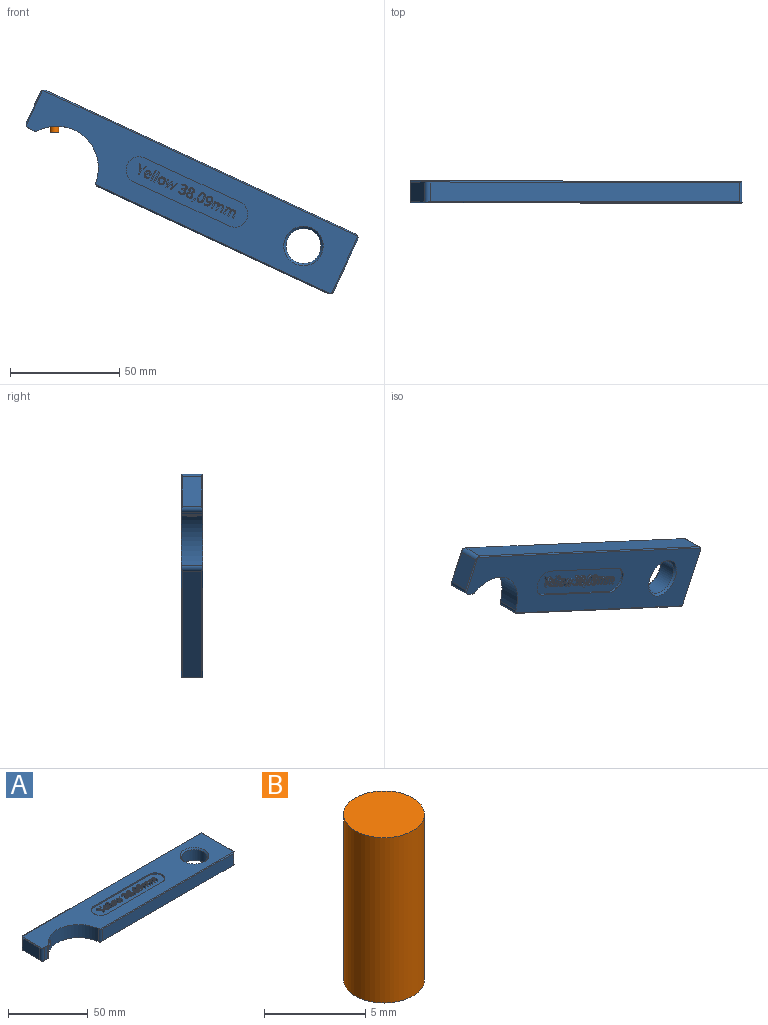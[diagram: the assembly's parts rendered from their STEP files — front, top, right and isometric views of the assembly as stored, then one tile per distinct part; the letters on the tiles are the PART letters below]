
ASSEMBLY  parts=2 mates=1
PART A: 291 faces, bbox 160x30x10 mm
  f0: cylinder r=19.04mm len=33.93mm, axis (0,0,-1), area 440.7mm2, adj f6,f7,f20,f25,f289
  f1: plane 60.11x12mm, normal (0,0,1), area 605.7mm2, adj f26,f27,f28,f29,f30,f31,f32,f33
  f2: plane 115.74x9mm, normal (0,-1,0), area 1041.6mm2, adj f10,f14,f20,f21
  f3: plane 26x9mm, normal (1,0,0), area 234mm2, adj f11,f15,f21,f22
  f4: plane 156x9mm, normal (0,1,0), area 1404mm2, adj f12,f16,f22,f23
  f5: plane 15x9mm, normal (-1,0,0), area 135mm2, adj f13,f17,f23,f24
  f6: plane 159x29mm, normal (0,0,1), area 3083.9mm2, adj f0,f8,f14,f15,f16,f17,f19,f20
  f7: plane 159x29mm, normal (0,0,-1), area 3774.3mm2, adj f0,f8,f10,f11,f12,f13,f18,f20
  f8: plane 10x2.76mm, normal (0,-1,0), area 27.6mm2, adj f6,f7,f24,f25
  f9: cylinder r=8mm len=16mm, axis (0,0,-1), area 402.1mm2, adj f18,f19
  f10: plane 118.38x0.5mm, normal (0,-0.71,-0.71), area 83.1mm2, adj f2,f7,f20,f21
  f11: plane 28.65x0.5mm, normal (0.71,0,-0.71), area 19.7mm2, adj f3,f7,f21,f22
  f12: plane 158.65x0.5mm, normal (0,0.71,-0.71), area 111.6mm2, adj f4,f7,f22,f23
  f13: plane 17.65x0.5mm, normal (-0.71,0,-0.71), area 11.9mm2, adj f5,f7,f23,f24
  f14: plane 118.38x0.5mm, normal (0,-0.71,0.71), area 83.1mm2, adj f2,f6,f20,f21
  f15: plane 28.65x0.5mm, normal (0.71,0,0.71), area 19.7mm2, adj f3,f6,f21,f22
  f16: plane 158.65x0.5mm, normal (0,0.71,0.71), area 111.6mm2, adj f4,f6,f22,f23
  f17: plane 17.65x0.5mm, normal (-0.71,0,0.71), area 11.9mm2, adj f5,f6,f23,f24
  f18: cone r=9mm half-angle=45deg, axis (0,0,-1), area 75.5mm2, adj f7,f9
  f19: cone r=8mm half-angle=45deg, axis (0,0,1), area 75.5mm2, adj f6,f9
  f20: cylinder r=2mm len=10mm, axis (0,0,-1), area 28.6mm2, adj f0,f2,f6,f7,f10,f14
  f21: cylinder r=2mm len=10mm, axis (0,0,1), area 29.5mm2, adj f2,f3,f6,f7,f10,f11,f14,f15
  f22: cylinder r=2mm len=10mm, axis (0,0,-1), area 29.5mm2, adj f3,f4,f6,f7,f11,f12,f15,f16
  f23: cylinder r=2mm len=10mm, axis (0,0,1), area 29.5mm2, adj f4,f5,f6,f7,f12,f13,f16,f17
  f24: cylinder r=2mm len=10mm, axis (0,0,1), area 30.5mm2, adj f5,f6,f7,f8,f13,f17
  f25: cylinder r=2mm len=10mm, axis (0,0,-1), area 18.1mm2, adj f0,f6,f7,f8
  f26: plane 48.11x1mm, normal (0,-1,0), area 48.1mm2, adj f1,f6,f27,f29
  f27: cylinder r=6mm len=12mm, axis (0,0,1), area 18.8mm2, adj f1,f6,f26,f28
  f28: plane 48.11x1mm, normal (0,1,0), area 48.1mm2, adj f1,f6,f27,f29
  f29: cylinder r=6mm len=12mm, axis (0,0,1), area 18.8mm2, adj f1,f6,f26,f28
  f30: plane 2.34x1.24mm, normal (-0.88,0.47,0), area 2.6mm2, adj f1,f31,f38,f39
  f31: plane 2.34x1.24mm, normal (0.88,0.47,0), area 2.6mm2, adj f1,f30,f32,f39
  f32: plane 1x0.59mm, normal (0,1,0), area 0.6mm2, adj f1,f31,f33,f39
  f33: plane 2.88x1.56mm, normal (-0.88,-0.47,0), area 3.3mm2, adj f1,f32,f34,f39
  f34: plane 1.79x1mm, normal (-1,0,0), area 1.8mm2, adj f1,f33,f35,f39
  f35: plane 1x0.55mm, normal (0,-1,0), area 0.5mm2, adj f1,f34,f36,f39
  f36: plane 1.81x1mm, normal (1,0,0), area 1.8mm2, adj f1,f35,f37,f39
  f37: plane 2.86x1.56mm, normal (0.88,-0.48,0), area 3.3mm2, adj f1,f36,f38,f39
  f38: plane 1x0.59mm, normal (0,1,0), area 0.6mm2, adj f1,f30,f37,f39
  f39: plane 4.67x3.66mm, normal (0,0,1), area 4.1mm2, adj f30,f31,f32,f33,f34,f35,f36,f37
  f40: extruded ~1x0.67mm, area 0.7mm2, adj f41,f58,f59,f60
  f41: extruded ~1x0.64mm, area 0.7mm2, adj f40,f42,f59,f60
  f42: extruded ~1x0.77mm, area 0.8mm2, adj f41,f43,f59,f60
  f43: plane 1.83x1mm, normal (0,1,0), area 1.8mm2, adj f42,f58,f59,f60
  f44: extruded ~1.22x1mm, area 1.4mm2, adj f1,f45,f57,f59
  f45: extruded ~1x0.61mm, area 0.6mm2, adj f1,f44,f46,f59
  f46: extruded ~1x0.53mm, area 0.6mm2, adj f1,f45,f47,f59
  f47: plane 1x0.47mm, normal (1,0,0), area 0.5mm2, adj f1,f46,f48,f59
  f48: extruded ~1.12x1mm, area 1.1mm2, adj f1,f47,f49,f59
  f49: extruded ~1x0.83mm, area 0.9mm2, adj f1,f48,f50,f59
  f50: extruded ~1x0.94mm, area 1mm2, adj f1,f49,f51,f59
  f51: plane 2.41x1mm, normal (0,-1,0), area 2.4mm2, adj f1,f50,f52,f59
  f52: plane 1x0.34mm, normal (1,0,0), area 0.3mm2, adj f1,f51,f53,f59
  f53: extruded ~1.14x1mm, area 1.2mm2, adj f1,f52,f54,f59
  f54: extruded ~1.04x1mm, area 1.2mm2, adj f1,f53,f55,f59
  f55: extruded ~1.12x1mm, area 1.3mm2, adj f1,f54,f56,f59
  f56: extruded ~1.35x1mm, area 1.4mm2, adj f1,f55,f57,f59
  f57: extruded ~1.31x1mm, area 1.4mm2, adj f1,f44,f56,f59
  f58: extruded ~1x0.76mm, area 0.8mm2, adj f40,f43,f59,f60
  f59: plane 3.63x2.96mm, normal (0,0,1), area 4.9mm2, adj f40,f41,f42,f43,f44,f45,f46,f47
  f60: plane 1.83x1.03mm, normal (0,0,1), area 1.5mm2, adj f40,f41,f42,f43,f58
  f61: plane 1x0.53mm, normal (0,-1,0), area 0.5mm2, adj f1,f62,f64,f65
  f62: plane 4.97x1mm, normal (1,0,0), area 5mm2, adj f1,f61,f63,f65
  f63: plane 1x0.53mm, normal (0,1,0), area 0.5mm2, adj f1,f62,f64,f65
  f64: plane 4.97x1mm, normal (-1,0,0), area 5mm2, adj f1,f61,f63,f65
  f65: plane 4.97x0.53mm, normal (0,0,1), area 2.6mm2, adj f61,f62,f63,f64
  f66: plane 1x0.53mm, normal (0,-1,0), area 0.5mm2, adj f1,f67,f69,f70
  f67: plane 4.97x1mm, normal (1,0,0), area 5mm2, adj f1,f66,f68,f70
  f68: plane 1x0.53mm, normal (0,1,0), area 0.5mm2, adj f1,f67,f69,f70
  f69: plane 4.97x1mm, normal (-1,0,0), area 5mm2, adj f1,f66,f68,f70
  f70: plane 4.97x0.53mm, normal (0,0,1), area 2.6mm2, adj f66,f67,f68,f69
  f71: extruded ~1.02x1mm, area 1.1mm2, adj f72,f87,f88,f89
  f72: extruded ~1.02x1mm, area 1.1mm2, adj f71,f73,f88,f89
  f73: extruded ~1x0.79mm, area 0.9mm2, adj f72,f74,f88,f89
  f74: extruded ~1x0.8mm, area 0.9mm2, adj f73,f75,f88,f89
  f75: extruded ~1.01x1mm, area 1.1mm2, adj f74,f76,f88,f89
  f76: extruded ~1.02x1mm, area 1.1mm2, adj f75,f77,f88,f89
  f77: extruded ~1x0.79mm, area 0.9mm2, adj f76,f87,f88,f89
  f78: extruded ~1.34x1mm, area 1.4mm2, adj f1,f79,f86,f88
  f79: extruded ~1.32x1mm, area 1.4mm2, adj f1,f78,f80,f88
  f80: extruded ~1.17x1mm, area 1.3mm2, adj f1,f79,f81,f88
  f81: extruded ~1.19x1mm, area 1.3mm2, adj f1,f80,f82,f88
  f82: extruded ~1.33x1mm, area 1.4mm2, adj f1,f81,f83,f88
  f83: extruded ~1x0.96mm, area 1mm2, adj f1,f82,f84,f88
  f84: extruded ~1x0.63mm, area 0.9mm2, adj f1,f83,f85,f88
  f85: extruded ~1x0.83mm, area 0.9mm2, adj f1,f84,f86,f88
  f86: extruded ~1.19x1mm, area 1.3mm2, adj f1,f78,f85,f88
  f87: extruded ~1x0.79mm, area 0.9mm2, adj f71,f77,f88,f89
  f88: plane 3.63x3.22mm, normal (0,0,1), area 4.7mm2, adj f71,f72,f73,f74,f75,f76,f77,f78
  f89: plane 2.73x2.12mm, normal (0,0,1), area 4.8mm2, adj f71,f72,f73,f74,f75,f76,f77,f87
  f90: plane 2.05x1mm, normal (-0.95,-0.3,0), area 2.2mm2, adj f1,f91,f112,f113
  f91: plane 1x0.63mm, normal (0,-1,0), area 0.6mm2, adj f1,f90,f92,f113
  f92: plane 3.5x1mm, normal (0.96,-0.27,0), area 3.6mm2, adj f1,f91,f93,f113
  f93: plane 1x0.55mm, normal (0,1,0), area 0.5mm2, adj f1,f92,f94,f113
  f94: extruded ~2.58x1mm, area 2.7mm2, adj f1,f93,f95,f113
  f95: extruded ~1x0.36mm, area 0.4mm2, adj f1,f94,f96,f113
  f96: plane 1x0.03mm, normal (0,1,0), area 0mm2, adj f1,f95,f97,f113
  f97: extruded ~1x0.92mm, area 1mm2, adj f1,f96,f98,f113
  f98: plane 2.01x1mm, normal (0.95,0.3,0), area 2.1mm2, adj f1,f97,f99,f113
  f99: plane 1x0.57mm, normal (0,1,0), area 0.6mm2, adj f1,f98,f100,f113
  f100: plane 2.01x1mm, normal (-0.95,0.3,0), area 2.1mm2, adj f1,f99,f101,f113
  f101: extruded ~1x0.46mm, area 0.5mm2, adj f1,f100,f102,f113
  f102: extruded ~1x0.47mm, area 0.5mm2, adj f1,f101,f103,f113
  f103: plane 1x0.03mm, normal (0,1,0), area 0mm2, adj f1,f102,f104,f113
  f104: extruded ~1x0.93mm, area 1mm2, adj f1,f103,f105,f113
  f105: extruded ~2.01x1mm, area 2.1mm2, adj f1,f104,f106,f113
  f106: plane 1x0.56mm, normal (0,1,0), area 0.6mm2, adj f1,f105,f107,f113
  f107: plane 3.5x1mm, normal (-0.96,-0.26,0), area 3.6mm2, adj f1,f106,f108,f113
  f108: plane 1x0.61mm, normal (0,-1,0), area 0.6mm2, adj f1,f107,f109,f113
  f109: plane 2.05x1mm, normal (0.95,-0.31,0), area 2.2mm2, adj f1,f108,f110,f113
  f110: extruded ~1x0.86mm, area 0.9mm2, adj f1,f109,f111,f113
  f111: plane 1x0.03mm, normal (0,-1,0), area 0mm2, adj f1,f110,f112,f113
  f112: extruded ~1x0.86mm, area 0.9mm2, adj f1,f90,f111,f113
  f113: plane 4.94x3.5mm, normal (0,0,1), area 6.7mm2, adj f90,f91,f92,f93,f94,f95,f96,f97
  f114: extruded ~1x0.73mm, area 0.8mm2, adj f1,f115,f141,f142
  f115: extruded ~1x0.85mm, area 1mm2, adj f1,f114,f116,f142
  f116: extruded ~1.06x1mm, area 1.1mm2, adj f1,f115,f117,f142
  f117: extruded ~1x0.79mm, area 0.8mm2, adj f1,f116,f118,f142
  f118: extruded ~1x0.66mm, area 0.8mm2, adj f1,f117,f119,f142
  f119: plane 1x0.36mm, normal (-0.8,-0.6,0), area 0.4mm2, adj f1,f118,f120,f142
  f120: extruded ~1x0.62mm, area 0.7mm2, adj f1,f119,f121,f142
  f121: extruded ~1x0.58mm, area 0.6mm2, adj f1,f120,f122,f142
  f122: extruded ~1x0.64mm, area 0.7mm2, adj f1,f121,f123,f142
  f123: extruded ~1x0.54mm, area 0.6mm2, adj f1,f122,f124,f142
  f124: extruded ~1x0.67mm, area 0.8mm2, adj f1,f123,f125,f142
  f125: extruded ~1x0.87mm, area 0.9mm2, adj f1,f124,f126,f142
  f126: plane 1x0.47mm, normal (0,1,0), area 0.5mm2, adj f1,f125,f127,f142
  f127: plane 1x0.46mm, normal (-1,0,0), area 0.5mm2, adj f1,f126,f128,f142
  f128: plane 1x0.46mm, normal (0,-1,0), area 0.5mm2, adj f1,f127,f129,f142
  f129: extruded ~1.33x1mm, area 1.8mm2, adj f1,f128,f130,f142
  f130: extruded ~1.21x1mm, area 1.8mm2, adj f1,f129,f131,f142
  f131: extruded ~1x0.65mm, area 0.7mm2, adj f1,f130,f132,f142
  f132: extruded ~1x0.65mm, area 0.7mm2, adj f1,f131,f133,f142
  f133: plane 1x0.51mm, normal (-1,0,0), area 0.5mm2, adj f1,f132,f134,f142
  f134: extruded ~1x0.6mm, area 0.6mm2, adj f1,f133,f135,f142
  f135: extruded ~1x0.68mm, area 0.7mm2, adj f1,f134,f136,f142
  f136: extruded ~1.32x1mm, area 1.4mm2, adj f1,f135,f137,f142
  f137: extruded ~1.03x1mm, area 1.2mm2, adj f1,f136,f138,f142
  f138: extruded ~1x0.75mm, area 0.8mm2, adj f1,f137,f139,f142
  f139: extruded ~1x0.83mm, area 0.9mm2, adj f1,f138,f140,f142
  f140: plane 1x0.03mm, normal (1,0,0), area 0mm2, adj f1,f139,f141,f142
  f141: extruded ~1x0.71mm, area 0.8mm2, adj f1,f114,f140,f142
  f142: plane 4.8x3.06mm, normal (0,0,1), area 5.1mm2, adj f114,f115,f116,f117,f118,f119,f120,f121
  f143: extruded ~1x0.63mm, area 0.7mm2, adj f144,f173,f174,f176
  f144: extruded ~1x0.64mm, area 0.7mm2, adj f143,f145,f174,f176
  f145: extruded ~1x0.51mm, area 0.6mm2, adj f144,f146,f174,f176
  f146: extruded ~1x0.51mm, area 0.6mm2, adj f145,f147,f174,f176
  f147: extruded ~1x0.65mm, area 0.8mm2, adj f146,f148,f174,f176
  f148: extruded ~1x0.7mm, area 0.8mm2, adj f147,f149,f174,f176
  f149: extruded ~1x0.5mm, area 0.6mm2, adj f148,f173,f174,f176
  f150: extruded ~1x0.6mm, area 0.7mm2, adj f151,f171,f174,f175
  f151: extruded ~1x0.59mm, area 0.6mm2, adj f150,f152,f174,f175
  f152: extruded ~1x0.69mm, area 0.8mm2, adj f151,f153,f174,f175
  f153: extruded ~1x0.87mm, area 1mm2, adj f152,f154,f174,f175
  f154: extruded ~1x0.55mm, area 0.6mm2, adj f153,f155,f174,f175
  f155: extruded ~1x0.61mm, area 0.7mm2, adj f154,f156,f174,f175
  f156: extruded ~1x0.74mm, area 0.8mm2, adj f155,f171,f174,f175
  f157: extruded ~1.01x1mm, area 1.1mm2, adj f1,f158,f172,f174
  f158: extruded ~1x1mm, area 1.1mm2, adj f1,f157,f159,f174
  f159: extruded ~1x0.81mm, area 0.9mm2, adj f1,f158,f160,f174
  f160: extruded ~1x0.65mm, area 0.7mm2, adj f1,f159,f161,f174
  f161: extruded ~1x0.63mm, area 0.8mm2, adj f1,f160,f162,f174
  f162: extruded ~1.25x1mm, area 1.7mm2, adj f1,f161,f163,f174
  f163: extruded ~1x0.93mm, area 1mm2, adj f1,f162,f164,f174
  f164: extruded ~1.15x1mm, area 1.2mm2, adj f1,f163,f165,f174
  f165: extruded ~1.11x1mm, area 1.2mm2, adj f1,f164,f166,f174
  f166: extruded ~1x0.93mm, area 1mm2, adj f1,f165,f167,f174
  f167: extruded ~1x0.69mm, area 0.7mm2, adj f1,f166,f168,f174
  f168: extruded ~1x0.81mm, area 1mm2, adj f1,f167,f169,f174
  f169: extruded ~1x0.68mm, area 0.9mm2, adj f1,f168,f170,f174
  f170: extruded ~1x0.63mm, area 0.7mm2, adj f1,f169,f172,f174
  f171: extruded ~1x0.75mm, area 0.8mm2, adj f150,f156,f174,f175
  f172: extruded ~1x0.82mm, area 0.9mm2, adj f1,f157,f170,f174
  f173: extruded ~1x0.51mm, area 0.6mm2, adj f143,f149,f174,f176
  f174: plane 4.8x3.07mm, normal (0,0,1), area 6.5mm2, adj f143,f144,f145,f146,f147,f148,f149,f150
  f175: plane 2.02x1.86mm, normal (0,0,1), area 2.9mm2, adj f150,f151,f152,f153,f154,f155,f156,f171
  f176: plane 1.72x1.63mm, normal (0,0,1), area 2.1mm2, adj f143,f144,f145,f146,f147,f148,f149,f173
  f177: plane 1x0.07mm, normal (0.84,0.55,0), area 0.1mm2, adj f1,f178,f183,f184
  f178: plane 1x0.58mm, normal (0,1,0), area 0.6mm2, adj f1,f177,f179,f184
  f179: extruded ~1x0.78mm, area 0.8mm2, adj f1,f178,f180,f184
  f180: extruded ~1x0.82mm, area 0.8mm2, adj f1,f179,f181,f184
  f181: plane 1x0.4mm, normal (0,-1,0), area 0.4mm2, adj f1,f180,f182,f184
  f182: extruded ~1x0.79mm, area 0.9mm2, adj f1,f181,f183,f184
  f183: extruded ~1x0.74mm, area 0.8mm2, adj f1,f177,f182,f184
  f184: plane 1.6x0.96mm, normal (0,0,1), area 0.9mm2, adj f177,f178,f179,f180,f181,f182,f183
  f185: extruded ~1.48x1mm, area 1.5mm2, adj f186,f200,f201,f202
  f186: extruded ~1.48x1mm, area 1.5mm2, adj f185,f187,f201,f202
  f187: extruded ~1x0.76mm, area 0.9mm2, adj f186,f188,f201,f202
  f188: extruded ~1x0.77mm, area 1mm2, adj f187,f189,f201,f202
  f189: extruded ~1.47x1mm, area 1.5mm2, adj f188,f190,f201,f202
  f190: extruded ~1.48x1mm, area 1.5mm2, adj f189,f191,f201,f202
  f191: extruded ~1x0.77mm, area 1mm2, adj f190,f200,f201,f202
  f192: extruded ~1.81x1mm, area 1.9mm2, adj f1,f193,f199,f201
  f193: extruded ~1.79x1mm, area 1.9mm2, adj f1,f192,f194,f201
  f194: extruded ~1.15x1mm, area 1.4mm2, adj f1,f193,f195,f201
  f195: extruded ~1.16x1mm, area 1.4mm2, adj f1,f194,f196,f201
  f196: extruded ~1.81x1mm, area 1.9mm2, adj f1,f195,f197,f201
  f197: extruded ~1.79x1mm, area 1.9mm2, adj f1,f196,f198,f201
  f198: extruded ~1.15x1mm, area 1.4mm2, adj f1,f197,f199,f201
  f199: extruded ~1.17x1mm, area 1.4mm2, adj f1,f192,f198,f201
  f200: extruded ~1x0.76mm, area 0.9mm2, adj f185,f191,f201,f202
  f201: plane 4.81x3.09mm, normal (0,0,1), area 5.8mm2, adj f185,f186,f187,f188,f189,f190,f191,f192
  f202: plane 3.89x2.01mm, normal (0,0,1), area 6.6mm2, adj f185,f186,f187,f188,f189,f190,f191,f200
  f203: extruded ~1x0.71mm, area 0.8mm2, adj f204,f228,f229,f230
  f204: extruded ~1x0.54mm, area 0.6mm2, adj f203,f205,f229,f230
  f205: extruded ~1x0.45mm, area 0.6mm2, adj f204,f206,f229,f230
  f206: extruded ~1x0.62mm, area 0.6mm2, adj f205,f207,f229,f230
  f207: extruded ~1x0.43mm, area 0.5mm2, adj f206,f208,f229,f230
  f208: extruded ~1x0.38mm, area 0.5mm2, adj f207,f209,f229,f230
  f209: extruded ~1x0.54mm, area 0.6mm2, adj f208,f210,f229,f230
  f210: extruded ~1x0.7mm, area 0.8mm2, adj f209,f211,f229,f230
  f211: extruded ~1x0.72mm, area 0.8mm2, adj f210,f228,f229,f230
  f212: extruded ~2.74x2.12mm, area 4mm2, adj f1,f213,f227,f229
  f213: extruded ~1.1x1mm, area 1.1mm2, adj f1,f212,f214,f229
  f214: extruded ~1x0.71mm, area 0.9mm2, adj f1,f213,f215,f229
  f215: extruded ~1x0.83mm, area 0.9mm2, adj f1,f214,f216,f229
  f216: extruded ~1.07x1mm, area 1.2mm2, adj f1,f215,f217,f229
  f217: extruded ~1.15x1mm, area 1.3mm2, adj f1,f216,f218,f229
  f218: extruded ~1.03x1mm, area 1.1mm2, adj f1,f217,f219,f229
  f219: extruded ~1x0.98mm, area 1.1mm2, adj f1,f218,f220,f229
  f220: extruded ~1x0.65mm, area 0.7mm2, adj f1,f219,f221,f229
  f221: extruded ~1x0.47mm, area 0.6mm2, adj f1,f220,f222,f229
  f222: plane 1x0.04mm, normal (0,-1,0), area 0mm2, adj f1,f221,f223,f229
  f223: extruded ~1.45x1mm, area 1.5mm2, adj f1,f222,f224,f229
  f224: extruded ~1.16x1mm, area 1.3mm2, adj f1,f223,f225,f229
  f225: extruded ~1x0.58mm, area 0.6mm2, adj f1,f224,f226,f229
  f226: plane 1x0.46mm, normal (-1,0,0), area 0.5mm2, adj f1,f225,f227,f229
  f227: extruded ~1x0.59mm, area 0.6mm2, adj f1,f212,f226,f229
  f228: extruded ~1x0.82mm, area 0.9mm2, adj f203,f211,f229,f230
  f229: plane 4.8x3.05mm, normal (0,0,1), area 5.7mm2, adj f203,f204,f205,f206,f207,f208,f209,f210
  f230: plane 2.1x1.99mm, normal (0,0,1), area 3.4mm2, adj f203,f204,f205,f206,f207,f208,f209,f210
  f231: plane 2.28x1mm, normal (-1,0,0), area 2.3mm2, adj f1,f232,f258,f259
  f232: plane 1x0.53mm, normal (0,-1,0), area 0.5mm2, adj f1,f231,f233,f259
  f233: plane 2.28x1mm, normal (1,0,0), area 2.3mm2, adj f1,f232,f234,f259
  f234: extruded ~1x0.98mm, area 1mm2, adj f1,f233,f235,f259
  f235: extruded ~1x0.89mm, area 1mm2, adj f1,f234,f236,f259
  f236: extruded ~1x0.68mm, area 0.7mm2, adj f1,f235,f237,f259
  f237: extruded ~1x0.45mm, area 0.6mm2, adj f1,f236,f238,f259
  f238: plane 1x0.03mm, normal (0,1,0), area 0mm2, adj f1,f237,f239,f259
  f239: extruded ~1.07x1mm, area 1.3mm2, adj f1,f238,f240,f259
  f240: extruded ~1x0.61mm, area 0.6mm2, adj f1,f239,f241,f259
  f241: extruded ~1x0.42mm, area 0.6mm2, adj f1,f240,f242,f259
  f242: plane 1x0.03mm, normal (0,1,0), area 0mm2, adj f1,f241,f243,f259
  f243: plane 1x0.48mm, normal (0.98,0.18,0), area 0.5mm2, adj f1,f242,f244,f259
  f244: plane 1x0.43mm, normal (0,1,0), area 0.4mm2, adj f1,f243,f245,f259
  f245: plane 3.5x1mm, normal (-1,0,0), area 3.5mm2, adj f1,f244,f246,f259
  f246: plane 1x0.53mm, normal (0,-1,0), area 0.5mm2, adj f1,f245,f247,f259
  f247: plane 1.84x1mm, normal (1,0,0), area 1.8mm2, adj f1,f246,f248,f259
  f248: extruded ~1x0.98mm, area 1mm2, adj f1,f247,f249,f259
  f249: extruded ~1x0.73mm, area 0.8mm2, adj f1,f248,f250,f259
  f250: extruded ~1x0.56mm, area 0.6mm2, adj f1,f249,f251,f259
  f251: extruded ~1x0.63mm, area 0.7mm2, adj f1,f250,f252,f259
  f252: plane 2.28x1mm, normal (-1,0,0), area 2.3mm2, adj f1,f251,f253,f259
  f253: plane 1x0.53mm, normal (0,-1,0), area 0.5mm2, adj f1,f252,f254,f259
  f254: plane 1.96x1mm, normal (1,0,0), area 2mm2, adj f1,f253,f255,f259
  f255: extruded ~1x0.87mm, area 0.9mm2, adj f1,f254,f256,f259
  f256: extruded ~1x0.73mm, area 0.8mm2, adj f1,f255,f257,f259
  f257: extruded ~1x0.56mm, area 0.6mm2, adj f1,f256,f258,f259
  f258: extruded ~1x0.63mm, area 0.7mm2, adj f1,f231,f257,f259
  f259: plane 4.99x3.56mm, normal (0,0,1), area 6.9mm2, adj f231,f232,f233,f234,f235,f236,f237,f238
  f260: plane 2.28x1mm, normal (-1,0,0), area 2.3mm2, adj f1,f261,f287,f288
  f261: plane 1x0.53mm, normal (0,-1,0), area 0.5mm2, adj f1,f260,f262,f288
  f262: plane 2.28x1mm, normal (1,0,0), area 2.3mm2, adj f1,f261,f263,f288
  f263: extruded ~1x0.98mm, area 1mm2, adj f1,f262,f264,f288
  f264: extruded ~1x0.89mm, area 1mm2, adj f1,f263,f265,f288
  f265: extruded ~1x0.68mm, area 0.7mm2, adj f1,f264,f266,f288
  f266: extruded ~1x0.45mm, area 0.6mm2, adj f1,f265,f267,f288
  f267: plane 1x0.03mm, normal (0,1,0), area 0mm2, adj f1,f266,f268,f288
  f268: extruded ~1.07x1mm, area 1.3mm2, adj f1,f267,f269,f288
  f269: extruded ~1x0.61mm, area 0.6mm2, adj f1,f268,f270,f288
  f270: extruded ~1x0.42mm, area 0.6mm2, adj f1,f269,f271,f288
  f271: plane 1x0.03mm, normal (0,1,0), area 0mm2, adj f1,f270,f272,f288
  f272: plane 1x0.48mm, normal (0.98,0.18,0), area 0.5mm2, adj f1,f271,f273,f288
  f273: plane 1x0.43mm, normal (0,1,0), area 0.4mm2, adj f1,f272,f274,f288
  f274: plane 3.5x1mm, normal (-1,0,0), area 3.5mm2, adj f1,f273,f275,f288
  f275: plane 1x0.53mm, normal (0,-1,0), area 0.5mm2, adj f1,f274,f276,f288
  f276: plane 1.84x1mm, normal (1,0,0), area 1.8mm2, adj f1,f275,f277,f288
  f277: extruded ~1x0.98mm, area 1mm2, adj f1,f276,f278,f288
  f278: extruded ~1x0.73mm, area 0.8mm2, adj f1,f277,f279,f288
  f279: extruded ~1x0.56mm, area 0.6mm2, adj f1,f278,f280,f288
  f280: extruded ~1x0.63mm, area 0.7mm2, adj f1,f279,f281,f288
  f281: plane 2.28x1mm, normal (-1,0,0), area 2.3mm2, adj f1,f280,f282,f288
  f282: plane 1x0.53mm, normal (0,-1,0), area 0.5mm2, adj f1,f281,f283,f288
  f283: plane 1.96x1mm, normal (1,0,0), area 2mm2, adj f1,f282,f284,f288
  f284: extruded ~1x0.87mm, area 0.9mm2, adj f1,f283,f285,f288
  f285: extruded ~1x0.73mm, area 0.8mm2, adj f1,f284,f286,f288
  f286: extruded ~1x0.56mm, area 0.6mm2, adj f1,f285,f287,f288
  f287: extruded ~1x0.63mm, area 0.7mm2, adj f1,f260,f286,f288
  f288: plane 4.99x3.56mm, normal (0,0,1), area 6.9mm2, adj f260,f261,f262,f263,f264,f265,f266,f267
  f289: cylinder r=2mm len=8.23mm, axis (-0.42,0.91,0), area 88.7mm2, adj f0,f290
  f290: plane 4x3.63mm, normal (0.42,-0.91,0), area 12.6mm2, adj f289
PART B: 3 faces, bbox 4x4x10 mm
  f0: cylinder r=2mm len=10mm, axis (0,0,-1), area 125.7mm2, adj f1,f2
  f1: plane 4x4mm, normal (0,0,1), area 12.6mm2, adj f0
  f2: plane 4x4mm, normal (0,0,-1), area 12.6mm2, adj f0
PLACE A rot(axis=(0.95,0.21,-0.21),92.7deg) t=(11.29,-30.31,-42.32)mm
PLACE B t=(-49.33,-35.31,-15.24)mm
MATE fastened A.f289 <-> B.f0  axis (0,0,-1) through (-49.33,-35.31,-5.24)mm
